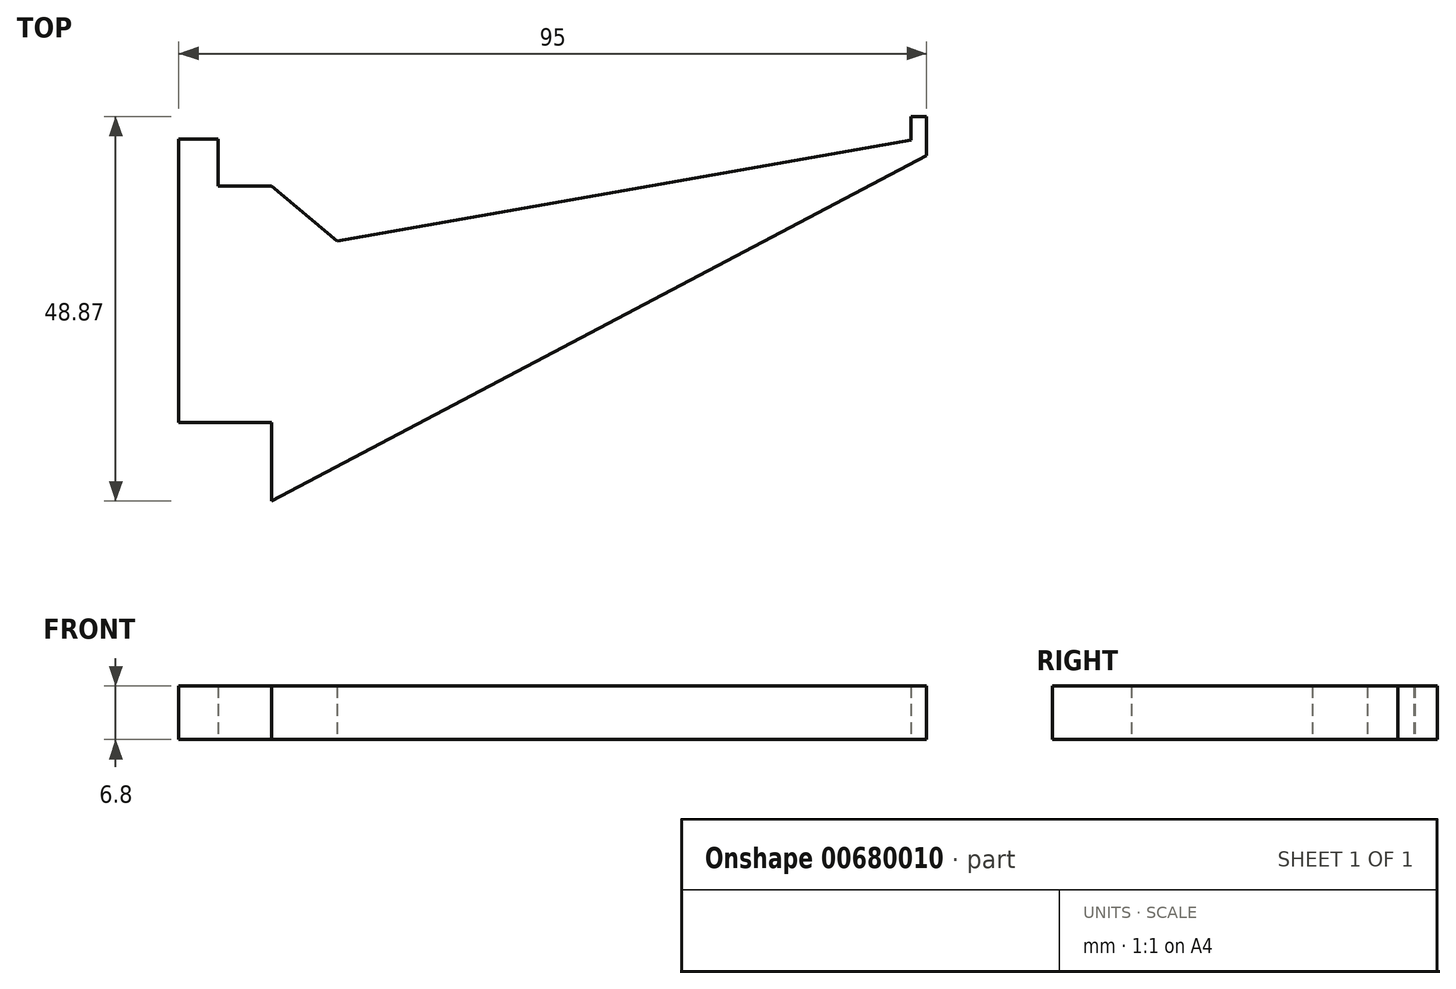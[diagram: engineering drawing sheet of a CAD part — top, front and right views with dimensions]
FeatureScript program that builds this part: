
annotation { "Feature Type Name" : "Feature", "Feature Type Description" : "" }
export const myFeature = defineFeature(function(context is Context, id is Id, definition is map)
    precondition{}
    {
        {
            var Q0;
            Q0=qCreatedBy(makeId("Top.planeOp"),FACE);
            var sketch = newSketch(context, id + "F0", { "sketchPlane" : qUnion([Q0])});
            skLineSegment(sketch, "E0", {"start": v(-6.8, 0) * mm, "end": v(0, 0) * mm});
            skLineSegment(sketch, "E1", {"start": v(-11.8, 36) * mm, "end": v(-11.8, 0) * mm});
            skLineSegment(sketch, "E2", {"start": v(0, 0) * mm, "end": v(0, 32) * mm, "construction": true});
            skLineSegment(sketch, "E3", {"start": v(0, 30) * mm, "end": v(-6.8, 30) * mm});
            skLineSegment(sketch, "E4", {"start": v(-6.8, 30) * mm, "end": v(-6.8, 36) * mm});
            skLineSegment(sketch, "E5", {"start": v(-6.8, 30) * mm, "end": v(-6.8, 0) * mm, "construction": true});
            skLineSegment(sketch, "E6", {"start": v(-11.8, 36) * mm, "end": v(-6.8, 36) * mm});
            skLineSegment(sketch, "E7", {"start": v(-6.8, 0) * mm, "end": v(-11.8, 0) * mm});
            skLineSegment(sketch, "E8", {"start": v(0, 0) * mm, "end": v(0, -10) * mm});
            skLineSegment(sketch, "E9", {"start": v(0, -10) * mm, "end": v(83.2, 33.87) * mm});
            skLineSegment(sketch, "E10", {"start": v(83.2, 33.87) * mm, "end": v(83.2, 38.87) * mm});
            skLineSegment(sketch, "E11", {"start": v(83.2, 38.87) * mm, "end": v(81.2, 38.87) * mm});
            skLineSegment(sketch, "E12", {"start": v(81.2, 38.87) * mm, "end": v(81.2, 35.87) * mm});
            skLineSegment(sketch, "E13", {"start": v(81.2, 35.87) * mm, "end": v(8.32, 23.02) * mm});
            skLineSegment(sketch, "E14", {"start": v(8.32, 23.02) * mm, "end": v(0, 30) * mm});
            skSolve(sketch);
        }
        {
            var Q0;
            Q0=qSketchRegion(id+"F0",true);
            extrude(context, id + "F1", {"entities" : qUnion([Q0]), "depth" : 6.8 * mm});
        }
    });
